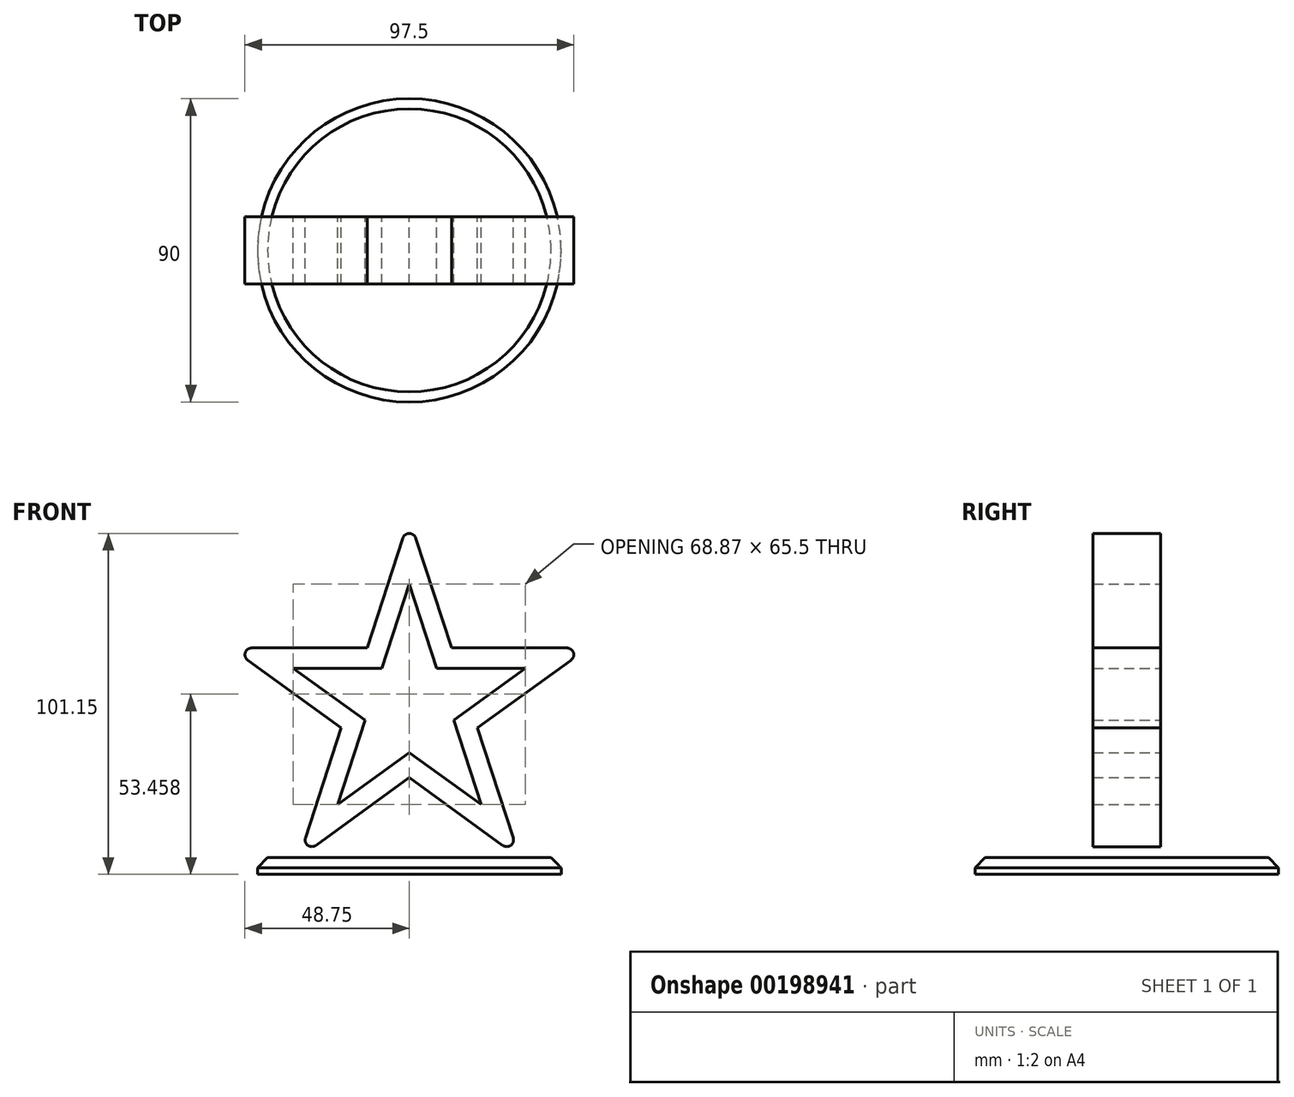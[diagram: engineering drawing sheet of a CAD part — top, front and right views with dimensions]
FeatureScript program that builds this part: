
annotation { "Feature Type Name" : "Feature", "Feature Type Description" : "" }
export const myFeature = defineFeature(function(context is Context, id is Id, definition is map)
    precondition{}
    {
        {
            var Q0;
            Q0=qCreatedBy(makeId("Top.planeOp"),FACE);
            var sketch = newSketch(context, id + "F0", { "sketchPlane" : qUnion([Q0])});
            skCircle(sketch, "E0", {"center": v(0, 0) * mm, "radius": 45 * mm});
            skSolve(sketch);
        }
        {
            var Q0;
            Q0 = qSketchRegion(id + "F0", true);
            extrude(context, id + "F1", {"entities" : qUnion([Q0]), "depth" : 5 * mm});
        }
        {
            var Q0;
            Q0=qCreatedBy(makeId("Front.planeOp"),FACE);
            var sketch = newSketch(context, id + "F2", { "sketchPlane" : qUnion([Q0])});
            skPoint(sketch, "E1", {"position": v(0, 50) * mm});
            skLineSegment(sketch, "E2.0", {"start": v(0, 5) * mm, "end": v(-32.7, 5) * mm});
            skPoint(sketch, "E2.0.midPoint", {"position": v(0, 5) * mm});
            skLineSegment(sketch, "E3", {"start": v(-52.9, 67.19) * mm, "end": v(-12.49, 67.19) * mm});
            skLineSegment(sketch, "E4", {"start": v(52.9, 67.19) * mm, "end": v(20.2, 43.43) * mm});
            skLineSegment(sketch, "E5", {"start": v(-32.7, 5) * mm, "end": v(-20.2, 43.43) * mm});
            skLineSegment(sketch, "E6", {"start": v(0, 105.62) * mm, "end": v(12.49, 67.19) * mm});
            skLineSegment(sketch, "E7", {"start": v(32.7, 5) * mm, "end": v(0, 28.75) * mm});
            skLineSegment(sketch, "E8.trimOffspring", {"start": v(12.49, 67.19) * mm, "end": v(52.9, 67.19) * mm});
            skLineSegment(sketch, "E9.trimOffspring", {"start": v(-12.49, 67.19) * mm, "end": v(0, 105.62) * mm});
            skLineSegment(sketch, "E10.trimOffspring", {"start": v(20.2, 43.43) * mm, "end": v(32.7, 5) * mm});
            skLineSegment(sketch, "E11.trimOffspring", {"start": v(0, 28.75) * mm, "end": v(-32.7, 5) * mm});
            skLineSegment(sketch, "E12.trimOffspring", {"start": v(-20.2, 43.43) * mm, "end": v(-52.9, 67.19) * mm});
            skLineSegment(sketch, "E13.0", {"start": v(-34.43, 61.19) * mm, "end": v(-8.13, 61.19) * mm});
            skLineSegment(sketch, "E13.1", {"start": v(-13.15, 45.73) * mm, "end": v(-34.43, 61.19) * mm});
            skLineSegment(sketch, "E13.2", {"start": v(-8.13, 61.19) * mm, "end": v(0, 86.2) * mm});
            skLineSegment(sketch, "E13.3", {"start": v(-21.28, 20.7) * mm, "end": v(-13.15, 45.73) * mm});
            skLineSegment(sketch, "E13.4", {"start": v(0, 36.17) * mm, "end": v(-21.28, 20.7) * mm});
            skLineSegment(sketch, "E13.5", {"start": v(21.28, 20.7) * mm, "end": v(0, 36.17) * mm});
            skLineSegment(sketch, "E13.6", {"start": v(0, 86.2) * mm, "end": v(8.13, 61.19) * mm});
            skLineSegment(sketch, "E13.7", {"start": v(8.13, 61.19) * mm, "end": v(34.43, 61.19) * mm});
            skLineSegment(sketch, "E13.8", {"start": v(34.43, 61.19) * mm, "end": v(13.15, 45.73) * mm});
            skLineSegment(sketch, "E13.9", {"start": v(13.15, 45.73) * mm, "end": v(21.28, 20.7) * mm});
            skLineSegment(sketch, "E14", {"start": v(32.7, 5) * mm, "end": v(27.7, 5) * mm});
            skLineSegment(sketch, "E15", {"start": v(27.7, 5) * mm, "end": v(27.7, 8.63) * mm});
            skLineSegment(sketch, "E16", {"start": v(-32.7, 5) * mm, "end": v(-27.7, 5) * mm});
            skLineSegment(sketch, "E17", {"start": v(-27.7, 5) * mm, "end": v(-27.7, 8.63) * mm});
            skSolve(sketch);
        }
        {
            var Q0;
            Q0=makeQuery(id+"F2.imprint","IMPRINT",FACE,{"disambiguationData":[TD([[makeQuery(id+"F2.imprint","IMPRINT",EDGE,{"derivedFrom":sQuery(id+"F2.wireOp",EDGE,"E3")}),-1.0]])]});
            extrude(context, id + "F3", {"entities" : qUnion([Q0]), "endBound" : BoundingType.SYMMETRIC, "depth" : 20 * mm});
        }
        {
            var Q0;
            Q0=makeQuery(id+"F1.opExtrude","CAP_EDGE",EDGE,{"disambiguationData":[OSD([sQuery(id+"F0.wireOp",EDGE,"E0")])],"isStart":false});
            chamfer(context, id + "F4", {"entities" : qUnion([Q0]), "width" : 3 * mm, "tangentPropagation" : true});
        }
        {
            var Q0;
            Q0=makeQuery(id+"F3.opExtrude","SWEPT_EDGE",EDGE,{"disambiguationData":[OSD([sQuery(id+"F2.wireOp",EDGE,"E6"),sQuery(id+"F2.wireOp",EDGE,"E9.trimOffspring")])]});
            var Q1;
            Q1=makeQuery(id+"F3.opExtrude","SWEPT_EDGE",EDGE,{"disambiguationData":[OSD([sQuery(id+"F2.wireOp",EDGE,"E4"),sQuery(id+"F2.wireOp",EDGE,"E8.trimOffspring")])]});
            var Q2;
            Q2=makeQuery(id+"F3.opExtrude","SWEPT_EDGE",EDGE,{"disambiguationData":[OSD([sQuery(id+"F2.wireOp",EDGE,"E7"),sQuery(id+"F2.wireOp",EDGE,"E10.trimOffspring")])]});
            var Q3;
            Q3=makeQuery(id+"F3.opExtrude","SWEPT_EDGE",EDGE,{"disambiguationData":[OSD([sQuery(id+"F2.wireOp",EDGE,"E5"),sQuery(id+"F2.wireOp",EDGE,"E11.trimOffspring")])]});
            var Q4;
            Q4=makeQuery(id+"F3.opExtrude","SWEPT_EDGE",EDGE,{"disambiguationData":[OSD([sQuery(id+"F2.wireOp",EDGE,"E3"),sQuery(id+"F2.wireOp",EDGE,"E12.trimOffspring")])]});
            fillet(context, id + "F5", {"entities" : qUnion([Q0, Q1, Q2, Q3, Q4]), "radius" : 2 * mm, "tangentPropagation" : true, "allowEdgeOverflow" : false});
        }
    });
